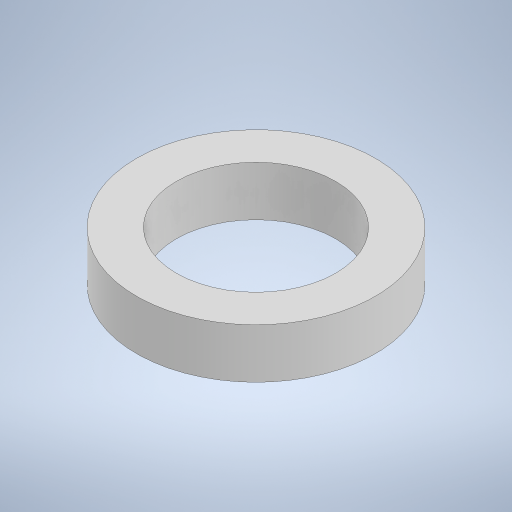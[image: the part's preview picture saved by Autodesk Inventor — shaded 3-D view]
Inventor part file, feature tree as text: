
AUTODESK INVENTOR PART (.ipt)
format: ipt  version: 2024 (Build 280153000, 153)  size: 217,088 bytes
history: native  units: mm
features: other x1, extrude x1, sketch x1
ambient origin geometry x8: Origin, YZ Plane, XZ Plane, XY Plane, X Axis, Y Axis, Z Axis, Center Point
bodies: Body1 (feature_tree)
feature tree (3):
  other  "솔리드1"
  extrude  "돌출1"  Depth=3.2mm
  sketch  "스케치1"
